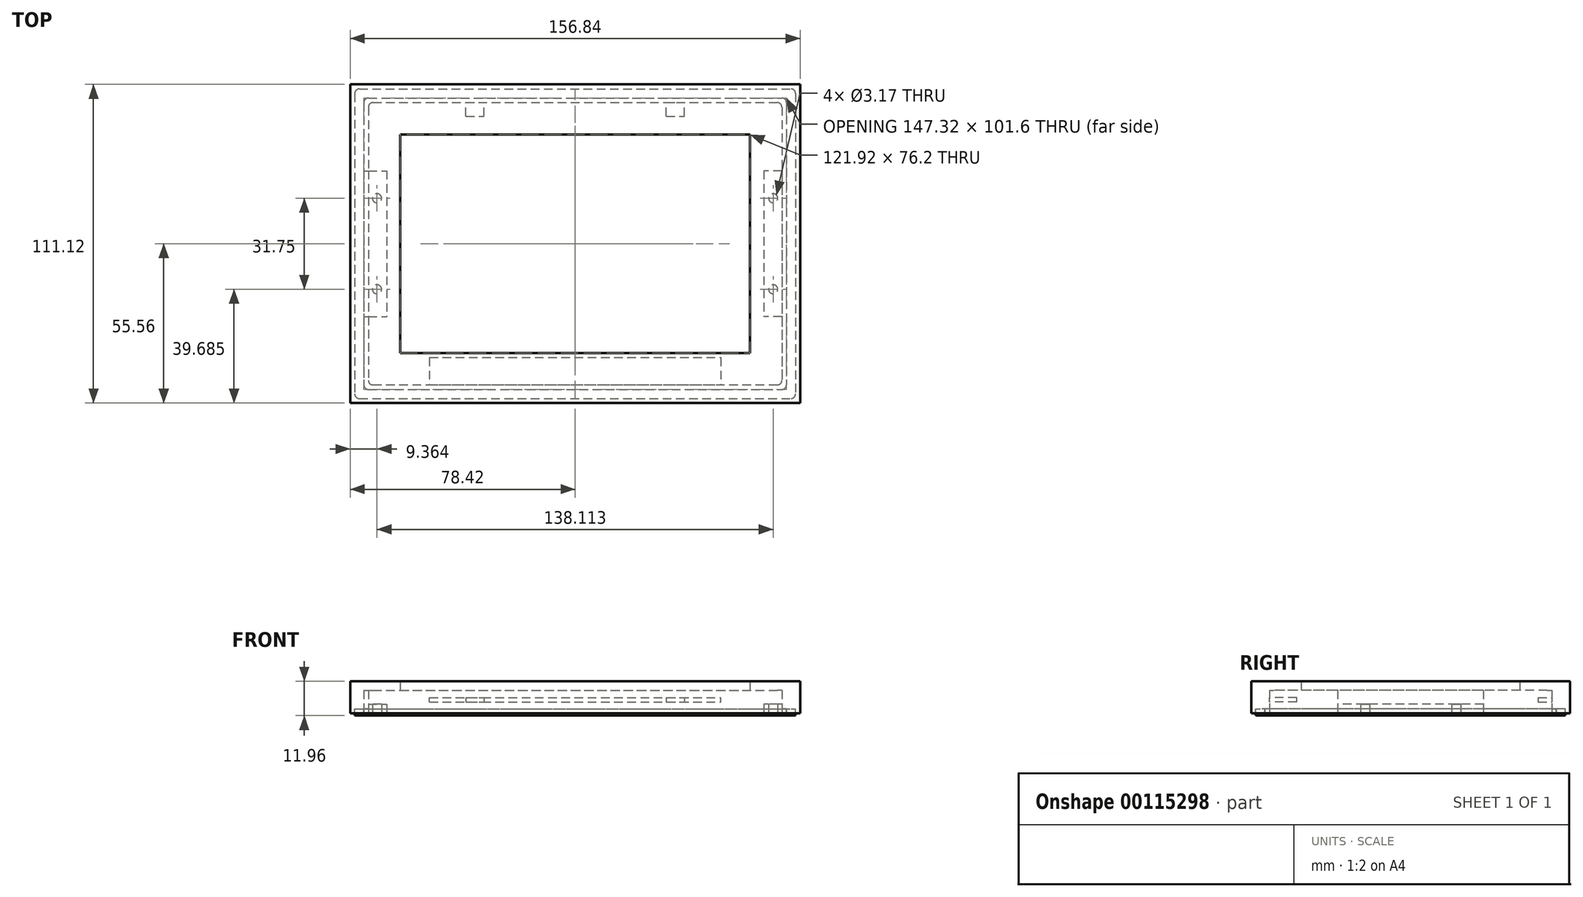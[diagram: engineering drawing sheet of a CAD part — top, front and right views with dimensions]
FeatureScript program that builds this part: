
annotation { "Feature Type Name" : "Feature", "Feature Type Description" : "" }
export const myFeature = defineFeature(function(context is Context, id is Id, definition is map)
    precondition{}
    {
        {
            var Q0;
            Q0=qCreatedBy(makeId("Top.planeOp"),FACE);
            var sketch = newSketch(context, id + "F0", { "sketchPlane" : qUnion([Q0])});
            skLineSegment(sketch, "E0.bottom", {"start": v(-72.07, 50.8) * mm, "end": v(72.07, 50.8) * mm});
            skLineSegment(sketch, "E0.top", {"start": v(-72.07, -50.8) * mm, "end": v(72.07, -50.8) * mm});
            skLineSegment(sketch, "E0.left", {"start": v(-73.66, 49.21) * mm, "end": v(-73.66, -49.21) * mm});
            skLineSegment(sketch, "E0.right", {"start": v(73.66, 49.21) * mm, "end": v(73.66, -49.21) * mm});
            skPoint(sketch, "E0.middle", {"position": v(0, 0) * mm});
            skLineSegment(sketch, "E1.bottom", {"start": v(-73.66, 25.4) * mm, "end": v(-65.72, 25.4) * mm});
            skLineSegment(sketch, "E1.top", {"start": v(-73.66, -25.4) * mm, "end": v(-65.72, -25.4) * mm});
            skLineSegment(sketch, "E1.left", {"start": v(-73.66, 25.4) * mm, "end": v(-73.66, -25.4) * mm});
            skLineSegment(sketch, "E1.right", {"start": v(-65.72, 25.4) * mm, "end": v(-65.72, -25.4) * mm});
            skPoint(sketch, "E2.centerSnap0", {"position": v(-69.7, 25.4) * mm});
            skPoint(sketch, "E3.centerSnap0", {"position": v(-69.7, -25.4) * mm});
            skLineSegment(sketch, "E4.0", {"start": v(-72.07, 49.21) * mm, "end": v(72.07, 49.21) * mm});
            skLineSegment(sketch, "E4.1", {"start": v(-72.07, 49.21) * mm, "end": v(-72.07, -49.21) * mm});
            skLineSegment(sketch, "E4.2", {"start": v(-72.07, -49.21) * mm, "end": v(72.07, -49.21) * mm});
            skLineSegment(sketch, "E4.3", {"start": v(72.07, 49.21) * mm, "end": v(72.07, -49.21) * mm});
            skLineSegment(sketch, "E5", {"start": v(72.07, 0) * mm, "end": v(-72.07, 0) * mm, "construction": true});
            skLineSegment(sketch, "E6", {"start": v(0, 49.21) * mm, "end": v(0, -49.21) * mm, "construction": true});
            skLineSegment(sketch, "E7.MirrorCS", {"start": v(65.72, 25.4) * mm, "end": v(65.72, -25.4) * mm});
            skLineSegment(sketch, "E8.MirrorCS", {"start": v(73.66, 25.4) * mm, "end": v(65.72, 25.4) * mm});
            skLineSegment(sketch, "E9.MirrorCS", {"start": v(73.66, -25.4) * mm, "end": v(65.72, -25.4) * mm});
            skCircle(sketch, "E10", {"center": v(69.06, 15.88) * mm, "radius": 1.59 * mm});
            skCircle(sketch, "E11", {"center": v(-69.06, 15.87) * mm, "radius": 1.59 * mm});
            skCircle(sketch, "E12.MirrorC", {"center": v(69.06, -15.87) * mm, "radius": 1.59 * mm});
            skCircle(sketch, "E13.MirrorC", {"center": v(-69.06, -15.88) * mm, "radius": 1.59 * mm});
            skLineSegment(sketch, "E14.0", {"start": v(-75.25, -53.98) * mm, "end": v(75.25, -53.98) * mm});
            skLineSegment(sketch, "E14.1", {"start": v(-76.84, 52.39) * mm, "end": v(-76.84, -52.39) * mm});
            skLineSegment(sketch, "E14.2", {"start": v(-75.25, 53.98) * mm, "end": v(75.25, 53.98) * mm});
            skLineSegment(sketch, "E14.3", {"start": v(76.83, 52.39) * mm, "end": v(76.83, -52.39) * mm});
            skLineSegment(sketch, "E15.0", {"start": v(-78.42, 55.56) * mm, "end": v(-78.42, -55.56) * mm});
            skLineSegment(sketch, "E15.1", {"start": v(-78.42, 55.56) * mm, "end": v(78.42, 55.56) * mm});
            skLineSegment(sketch, "E15.2", {"start": v(78.42, 55.56) * mm, "end": v(78.42, -55.56) * mm});
            skLineSegment(sketch, "E15.3", {"start": v(-78.42, -55.56) * mm, "end": v(78.42, -55.56) * mm});
            skPoint(sketch, "E16.visualSharp", {"position": v(73.66, 50.8) * mm});
            skArc(sketch, "E16.filletArc", {"start": v(73.66, 49.21) * mm, "mid": v(73.2, 50.34) * mm, "end": v(72.07, 50.8) * mm});
            skPoint(sketch, "E17.visualSharp", {"position": v(76.84, 53.98) * mm});
            skArc(sketch, "E17.filletArc", {"start": v(76.84, 52.39) * mm, "mid": v(76.37, 53.51) * mm, "end": v(75.25, 53.97) * mm});
            skPoint(sketch, "E18.visualSharp", {"position": v(-73.66, 50.8) * mm});
            skArc(sketch, "E18.filletArc", {"start": v(-72.07, 50.8) * mm, "mid": v(-73.2, 50.34) * mm, "end": v(-73.66, 49.21) * mm});
            skPoint(sketch, "E19.visualSharp", {"position": v(-76.84, 53.97) * mm});
            skArc(sketch, "E19.filletArc", {"start": v(-75.25, 53.98) * mm, "mid": v(-76.37, 53.51) * mm, "end": v(-76.84, 52.39) * mm});
            skPoint(sketch, "E20.visualSharp", {"position": v(73.66, -50.8) * mm});
            skArc(sketch, "E20.filletArc", {"start": v(72.07, -50.8) * mm, "mid": v(73.2, -50.34) * mm, "end": v(73.66, -49.21) * mm});
            skPoint(sketch, "E21.visualSharp", {"position": v(76.83, -53.98) * mm});
            skArc(sketch, "E21.filletArc", {"start": v(75.25, -53.98) * mm, "mid": v(76.37, -53.51) * mm, "end": v(76.83, -52.39) * mm});
            skPoint(sketch, "E22.visualSharp", {"position": v(-73.66, -50.8) * mm});
            skArc(sketch, "E22.filletArc", {"start": v(-73.66, -49.21) * mm, "mid": v(-73.2, -50.34) * mm, "end": v(-72.07, -50.8) * mm});
            skPoint(sketch, "E23.visualSharp", {"position": v(-76.84, -53.98) * mm});
            skArc(sketch, "E23.filletArc", {"start": v(-76.84, -52.39) * mm, "mid": v(-76.37, -53.51) * mm, "end": v(-75.25, -53.98) * mm});
            skSolve(sketch);
        }
        {
            var Q0;
            Q0 = qSketchRegion(id + "F0", true);
            var Q1;
            {var subQ6=sQuery(id+"F0.wireOp",EDGE,"E0.top");Q1=makeQuery(id+"F0.imprint","IMPRINT",FACE,{"disambiguationData":[TD([[makeQuery(id+"F0.imprint","IMPRINT",EDGE,{"derivedFrom":subQ6}),1.0]])]});}
            var Q2;
            {var subQ10=sQuery(id+"F0.wireOp",EDGE,"E0.bottom");Q2=makeQuery(id+"F0.imprint","IMPRINT",FACE,{"disambiguationData":[TD([[makeQuery(id+"F0.imprint","IMPRINT",EDGE,{"derivedFrom":subQ10}),-1.0]])]});}
            var Q3;
            {var subQ0=sQuery(id+"F0.wireOp",EDGE,"E1.left");Q3=makeQuery(id+"F0.imprint","IMPRINT",FACE,{"disambiguationData":[TD([[makeQuery(id+"F0.imprint","IMPRINT",EDGE,{"derivedFrom":subQ0}),1.0]])]});}
            var Q4;
            {var subQ0=sQuery(id+"F0.wireOp",EDGE,"E8.MirrorCS");var subQ1=sQuery(id+"F0.wireOp",EDGE,"E0.right");var subQ2=makeQuery(id+"F0.imprint","INTERSECT",VERTEX,{"derivedFrom":[subQ1,subQ0]});Q4=makeQuery(id+"F0.imprint","IMPRINT",FACE,{"disambiguationData":[TD([[makeQuery(id+"F0.imprint","IMPRINT",EDGE,{"disambiguationData":[TD([[subQ2,-1.0]])],"derivedFrom":subQ1}),-1.0]])]});}
            var Q5;
            {var subQ5=sQuery(id+"F0.wireOp",EDGE,"E0.bottom");Q5=makeQuery(id+"F0.imprint","IMPRINT",FACE,{"disambiguationData":[TD([[makeQuery(id+"F0.imprint","IMPRINT",EDGE,{"derivedFrom":subQ5}),1.0]])]});}
            extrude(context, id + "F1", {"entities" : qUnion([Q0, Q1, Q2, Q3, Q4, Q5]), "depth" : 8 * mm});
        }
        {
            var Q0;
            {var subQ1=sQuery(id+"F0.wireOp",EDGE,"E7.MirrorCS");Q0=makeQuery(id+"F0.imprint","IMPRINT",FACE,{"disambiguationData":[TD([[makeQuery(id+"F0.imprint","IMPRINT",EDGE,{"derivedFrom":subQ1}),1.0]])]});}
            var Q1;
            {var subQ0=sQuery(id+"F0.wireOp",EDGE,"E1.right");Q1=makeQuery(id+"F0.imprint","IMPRINT",FACE,{"disambiguationData":[TD([[makeQuery(id+"F0.imprint","IMPRINT",EDGE,{"derivedFrom":subQ0}),-1.0]])]});}
            extrude(context, id + "F2", {"entities" : qUnion([Q0, Q1]), "operationType" : NewBodyOperationType.ADD, "depth" : 3.17 * mm});
        }
        {
            var Q0;
            Q0=makeQuery(id+"F1.opExtrude","CAP_FACE",FACE,{"disambiguationData":[OSD([sQuery(id+"F0.wireOp",EDGE,"E0.bottom"),sQuery(id+"F0.wireOp",EDGE,"E0.top"),sQuery(id+"F0.wireOp",EDGE,"E0.left"),sQuery(id+"F0.wireOp",EDGE,"E0.right"),sQuery(id+"F0.wireOp",EDGE,"E1.left"),sQuery(id+"F0.wireOp",EDGE,"E4.0"),sQuery(id+"F0.wireOp",EDGE,"E4.1"),sQuery(id+"F0.wireOp",EDGE,"E4.2"),sQuery(id+"F0.wireOp",EDGE,"E4.3")])],"isStart":false});
            var sketch = newSketch(context, id + "F3", { "sketchPlane" : qUnion([Q0])});
            skLineSegment(sketch, "E24.0", {"start": v(-60.96, 38.1) * mm, "end": v(-60.96, -38.1) * mm});
            skLineSegment(sketch, "E24.1", {"start": v(-60.96, 38.1) * mm, "end": v(60.96, 38.1) * mm});
            skLineSegment(sketch, "E24.2", {"start": v(60.96, 38.1) * mm, "end": v(60.96, -38.1) * mm});
            skLineSegment(sketch, "E24.3", {"start": v(-60.96, -38.1) * mm, "end": v(60.96, -38.1) * mm});
            skSolve(sketch);
        }
        {
            var Q0;
            Q0=makeQuery(id+"F3.imprint","IMPRINT",FACE,{"disambiguationData":[TD([[makeQuery(id+"F3.imprint","IMPRINT",EDGE,{"derivedFrom":sQuery(id+"F3.wireOp",EDGE,"E24.0")}),-1.0]])]});
            var Q1;
            Q1=makeQuery(id+"F3.imprint","IMPRINT",FACE,{"disambiguationData":[TD([[makeQuery(id+"F3.imprint","IMPRINT",EDGE,{"derivedFrom":makeQuery(id+"F1.opExtrude","CAP_EDGE",EDGE,{"disambiguationData":[OSD([sQuery(id+"F0.wireOp",EDGE,"E0.bottom")])],"isStart":false})}),-1.0]])]});
            var Q2;
            Q2=makeQuery(id+"F3.imprint","IMPRINT",FACE,{"disambiguationData":[TD([[makeQuery(id+"F3.imprint","IMPRINT",EDGE,{"derivedFrom":makeQuery(id+"F1.opExtrude","CAP_EDGE",EDGE,{"disambiguationData":[OSD([sQuery(id+"F0.wireOp",EDGE,"E4.0")])],"isStart":false})}),1.0]])]});
            extrude(context, id + "F4", {"entities" : qUnion([Q0, Q1, Q2]), "operationType" : NewBodyOperationType.ADD, "depth" : 3.17 * mm});
        }
        {
            var Q0;
            {var subQ0=sQuery(id+"F0.wireOp",EDGE,"E0.right");var subQ1=sQuery(id+"F0.wireOp",EDGE,"E0.bottom");Q0=makeQuery(id+"F4.boolean.opBoolean","MERGE",EDGE,{"derivedFrom":[makeQuery(id+"F1.opExtrude","SWEPT_EDGE",EDGE,{"disambiguationData":[OSD([subQ1,subQ0])]}),makeQuery(id+"F4.opExtrude","SWEPT_EDGE",EDGE,{"disambiguationData":[OSD([subQ1,subQ0])]})]});}
            var Q1;
            {var subQ0=sQuery(id+"F0.wireOp",EDGE,"E0.left");var subQ1=sQuery(id+"F0.wireOp",EDGE,"E0.bottom");Q1=makeQuery(id+"F4.boolean.opBoolean","MERGE",EDGE,{"derivedFrom":[makeQuery(id+"F1.opExtrude","SWEPT_EDGE",EDGE,{"disambiguationData":[OSD([subQ1,subQ0])]}),makeQuery(id+"F4.opExtrude","SWEPT_EDGE",EDGE,{"disambiguationData":[OSD([subQ1,subQ0,sQuery(id+"F0.wireOp",EDGE,"E1.left")])]})]});}
            var Q2;
            {var subQ0=sQuery(id+"F0.wireOp",EDGE,"E0.left");var subQ1=sQuery(id+"F0.wireOp",EDGE,"E0.top");Q2=makeQuery(id+"F4.boolean.opBoolean","MERGE",EDGE,{"derivedFrom":[makeQuery(id+"F1.opExtrude","SWEPT_EDGE",EDGE,{"disambiguationData":[OSD([subQ1,subQ0])]}),makeQuery(id+"F4.opExtrude","SWEPT_EDGE",EDGE,{"disambiguationData":[OSD([subQ1,subQ0,sQuery(id+"F0.wireOp",EDGE,"E1.left")])]})]});}
            var Q3;
            {var subQ0=sQuery(id+"F0.wireOp",EDGE,"E0.right");var subQ1=sQuery(id+"F0.wireOp",EDGE,"E0.top");Q3=makeQuery(id+"F4.boolean.opBoolean","MERGE",EDGE,{"derivedFrom":[makeQuery(id+"F1.opExtrude","SWEPT_EDGE",EDGE,{"disambiguationData":[OSD([subQ1,subQ0])]}),makeQuery(id+"F4.opExtrude","SWEPT_EDGE",EDGE,{"disambiguationData":[OSD([subQ1,subQ0])]})]});}
            var Q4;
            Q4=makeQuery(id+"F1.opExtrude","SWEPT_EDGE",EDGE,{"disambiguationData":[OSD([sQuery(id+"F0.wireOp",EDGE,"E4.1"),sQuery(id+"F0.wireOp",EDGE,"E4.2")])]});
            var Q5;
            Q5=makeQuery(id+"F1.opExtrude","SWEPT_EDGE",EDGE,{"disambiguationData":[OSD([sQuery(id+"F0.wireOp",EDGE,"E4.0"),sQuery(id+"F0.wireOp",EDGE,"E4.1")])]});
            var Q6;
            Q6=makeQuery(id+"F1.opExtrude","SWEPT_EDGE",EDGE,{"disambiguationData":[OSD([sQuery(id+"F0.wireOp",EDGE,"E4.2"),sQuery(id+"F0.wireOp",EDGE,"E4.3")])]});
            var Q7;
            Q7=makeQuery(id+"F1.opExtrude","SWEPT_EDGE",EDGE,{"disambiguationData":[OSD([sQuery(id+"F0.wireOp",EDGE,"E4.0"),sQuery(id+"F0.wireOp",EDGE,"E4.3")])]});
            fillet(context, id + "F5", {"entities" : qUnion([Q0, Q1, Q2, Q3, Q4, Q5, Q6, Q7]), "radius" : 1.59 * mm, "tangentPropagation" : true, "allowEdgeOverflow" : false});
        }
        {
            var Q0;
            Q0=makeQuery(id+"F1.opExtrude","SWEPT_FACE",FACE,{"disambiguationData":[OSD([sQuery(id+"F0.wireOp",EDGE,"E4.2")])]});
            var sketch = newSketch(context, id + "F6", { "sketchPlane" : qUnion([Q0])});
            skLineSegment(sketch, "E25.0", {"start": v(70.48, 5.5) * mm, "end": v(-70.48, 5.5) * mm});
            skLineSegment(sketch, "E26.0", {"start": v(70.48, 3.91) * mm, "end": v(-70.48, 3.91) * mm});
            skLineSegment(sketch, "E27", {"start": v(50.8, 3.91) * mm, "end": v(50.8, 5.5) * mm});
            skLineSegment(sketch, "E28", {"start": v(0, 0) * mm, "end": v(0, 8) * mm, "construction": true});
            skLineSegment(sketch, "E29.MirrorCS", {"start": v(-50.8, 3.91) * mm, "end": v(-50.8, 5.5) * mm});
            skSolve(sketch);
        }
        {
            var Q0;
            {var subQ0=sQuery(id+"F6.wireOp",EDGE,"E27");Q0=makeQuery(id+"F6.imprint","IMPRINT",FACE,{"disambiguationData":[TD([[makeQuery(id+"F6.imprint","IMPRINT",EDGE,{"derivedFrom":subQ0}),1.0]])]});}
            extrude(context, id + "F7", {"entities" : qUnion([Q0]), "operationType" : NewBodyOperationType.ADD, "depth" : 9.52 * mm});
        }
        {
            var Q0;
            Q0=makeQuery(id+"F1.opExtrude","SWEPT_FACE",FACE,{"disambiguationData":[OSD([sQuery(id+"F0.wireOp",EDGE,"E4.0")])]});
            var sketch = newSketch(context, id + "F8", { "sketchPlane" : qUnion([Q0])});
            skLineSegment(sketch, "E30.0", {"start": v(-70.48, 5.5) * mm, "end": v(70.48, 5.5) * mm});
            skLineSegment(sketch, "E31.0", {"start": v(-70.48, 3.91) * mm, "end": v(70.48, 3.91) * mm});
            skLineSegment(sketch, "E32", {"start": v(0, 8) * mm, "end": v(0, 0) * mm, "construction": true});
            skLineSegment(sketch, "E33", {"start": v(-38.1, 5.5) * mm, "end": v(-38.1, 3.91) * mm});
            skLineSegment(sketch, "E34", {"start": v(-31.75, 5.5) * mm, "end": v(-31.75, 3.91) * mm});
            skLineSegment(sketch, "E35.MirrorCS", {"start": v(38.1, 5.5) * mm, "end": v(38.1, 3.91) * mm});
            skLineSegment(sketch, "E36.MirrorCS", {"start": v(31.75, 5.5) * mm, "end": v(31.75, 3.91) * mm});
            skSolve(sketch);
        }
        {
            var Q0;
            {var subQ0=sQuery(id+"F8.wireOp",EDGE,"E33");Q0=makeQuery(id+"F8.imprint","IMPRINT",FACE,{"disambiguationData":[TD([[makeQuery(id+"F8.imprint","IMPRINT",EDGE,{"derivedFrom":subQ0}),1.0]])]});}
            var Q1;
            {var subQ0=sQuery(id+"F8.wireOp",EDGE,"E35.MirrorCS");Q1=makeQuery(id+"F8.imprint","IMPRINT",FACE,{"disambiguationData":[TD([[makeQuery(id+"F8.imprint","IMPRINT",EDGE,{"derivedFrom":subQ0}),-1.0]])]});}
            extrude(context, id + "F9", {"entities" : qUnion([Q0, Q1]), "operationType" : NewBodyOperationType.ADD, "depth" : 4.76 * mm});
        }
        {
            var Q0;
            {var subQ5=sQuery(id+"F0.wireOp",EDGE,"E0.bottom");Q0=makeQuery(id+"F0.imprint","IMPRINT",FACE,{"disambiguationData":[TD([[makeQuery(id+"F0.imprint","IMPRINT",EDGE,{"derivedFrom":subQ5}),1.0]])]});}
            extrude(context, id + "F10", {"entities" : qUnion([Q0]), "operationType" : NewBodyOperationType.REMOVE, "depth" : 1.59 * mm});
        }
        {
            var Q0;
            Q0=makeQuery(id+"F10.boolean.opBoolean","COPY",FACE,{"derivedFrom":makeQuery(id+"F10.opExtrude","CAP_FACE",FACE,{"disambiguationData":[OSD([sQuery(id+"F0.wireOp",EDGE,"E0.bottom"),sQuery(id+"F0.wireOp",EDGE,"E0.top"),sQuery(id+"F0.wireOp",EDGE,"E0.left"),sQuery(id+"F0.wireOp",EDGE,"E0.right"),sQuery(id+"F0.wireOp",EDGE,"E1.left"),sQuery(id+"F0.wireOp",EDGE,"E14.0"),sQuery(id+"F0.wireOp",EDGE,"E14.1"),sQuery(id+"F0.wireOp",EDGE,"E14.2"),sQuery(id+"F0.wireOp",EDGE,"E14.3"),sQuery(id+"F0.wireOp",EDGE,"E16.filletArc"),sQuery(id+"F0.wireOp",EDGE,"E17.filletArc"),sQuery(id+"F0.wireOp",EDGE,"E18.filletArc"),sQuery(id+"F0.wireOp",EDGE,"E19.filletArc"),sQuery(id+"F0.wireOp",EDGE,"E20.filletArc"),sQuery(id+"F0.wireOp",EDGE,"E21.filletArc"),sQuery(id+"F0.wireOp",EDGE,"E22.filletArc"),sQuery(id+"F0.wireOp",EDGE,"E23.filletArc")])],"isStart":false})});
            extrude(context, id + "F11", {"entities" : qUnion([Q0]), "depth" : 2.38 * mm});
        }
    });
